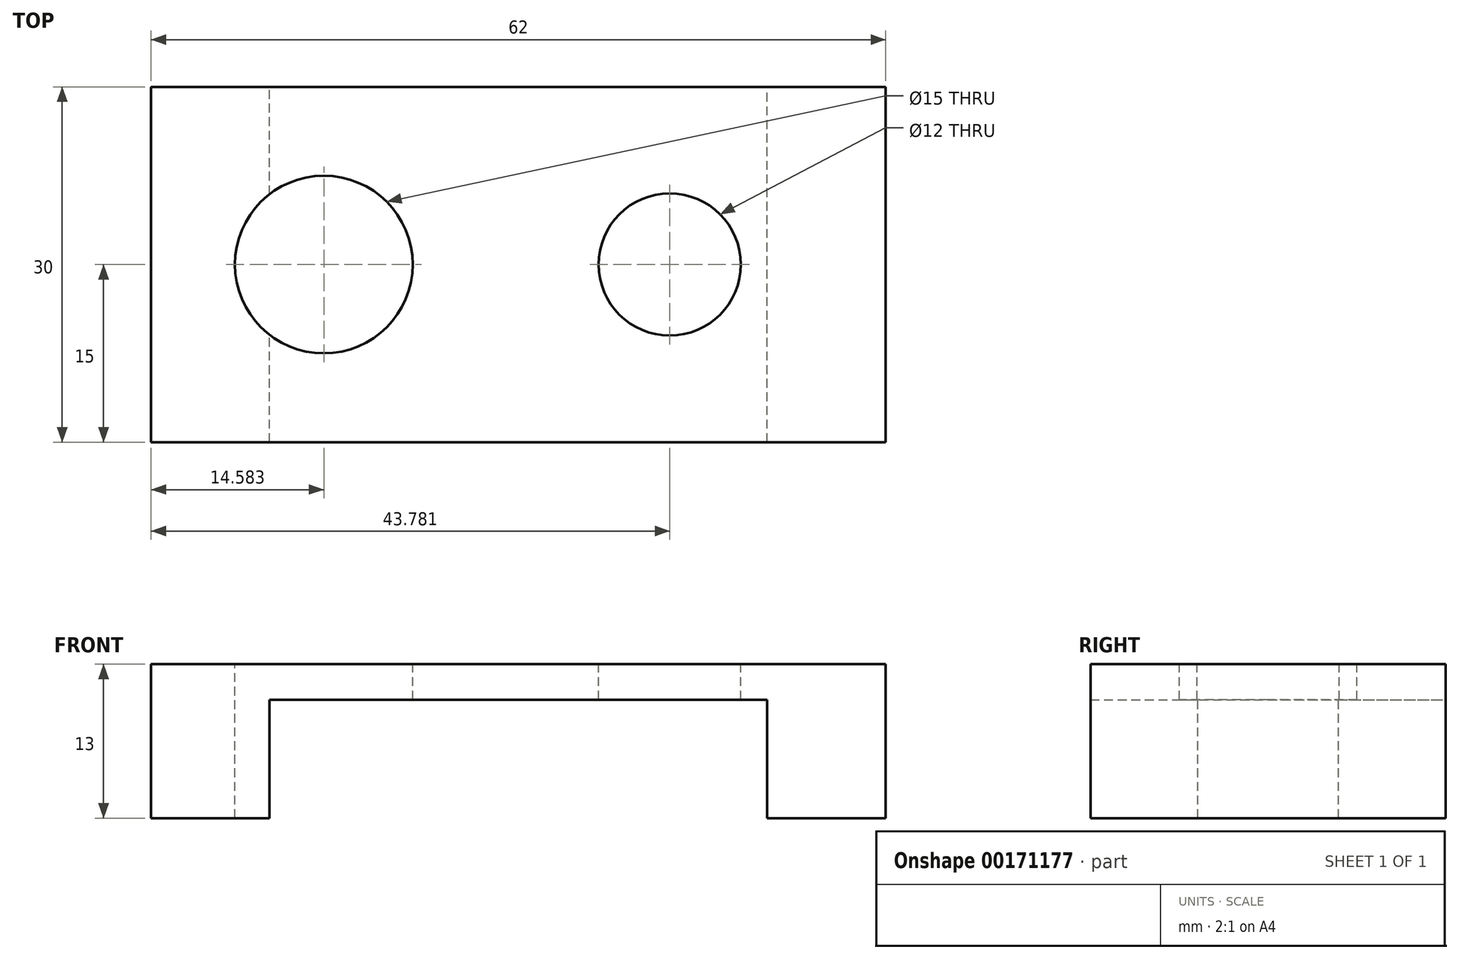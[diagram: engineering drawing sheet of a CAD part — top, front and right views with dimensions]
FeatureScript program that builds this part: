
annotation { "Feature Type Name" : "Feature", "Feature Type Description" : "" }
export const myFeature = defineFeature(function(context is Context, id is Id, definition is map)
    precondition{}
    {
        {
            var Q0;
            Q0=qCreatedBy(makeId("Front.planeOp"),FACE);
            var sketch = newSketch(context, id + "F0", { "sketchPlane" : qUnion([Q0])});
            skLineSegment(sketch, "E0", {"start": v(0, 0) * mm, "end": v(62, 0) * mm});
            skLineSegment(sketch, "E1", {"start": v(62, 0) * mm, "end": v(62, -13) * mm});
            skLineSegment(sketch, "E2", {"start": v(62, -13) * mm, "end": v(52, -13) * mm});
            skLineSegment(sketch, "E3", {"start": v(52, -13) * mm, "end": v(52, -3) * mm});
            skLineSegment(sketch, "E4", {"start": v(52, -3) * mm, "end": v(10, -3) * mm});
            skLineSegment(sketch, "E5", {"start": v(10, -3) * mm, "end": v(10, -13) * mm});
            skLineSegment(sketch, "E6", {"start": v(10, -13) * mm, "end": v(0, -13) * mm});
            skLineSegment(sketch, "E7", {"start": v(0, -13) * mm, "end": v(0, 0) * mm});
            skSolve(sketch);
        }
        {
            var Q0;
            Q0 = qSketchRegion(id + "F0", true);
            extrude(context, id + "F1", {"entities" : qUnion([Q0]), "depth" : 30 * mm});
        }
        {
            var Q0;
            Q0=makeQuery(id+"F1.opExtrude","SWEPT_FACE",FACE,{"disambiguationData":[OSD([sQuery(id+"F0.wireOp",EDGE,"E0")])]});
            var sketch = newSketch(context, id + "F2", { "sketchPlane" : qUnion([Q0])});
            skCircle(sketch, "E8", {"center": v(43.78, -15) * mm, "radius": 6 * mm});
            skCircle(sketch, "E9", {"center": v(14.58, -15) * mm, "radius": 7.5 * mm});
            skSolve(sketch);
        }
        {
            var Q0;
            Q0 = qSketchRegion(id + "F2", true);
            extrude(context, id + "F3", {"entities" : qUnion([Q0]), "operationType" : NewBodyOperationType.REMOVE, "endBound" : BoundingType.THROUGH_ALL, "oppositeDirection" : true, "depth" : 25 * mm});
        }
    });
